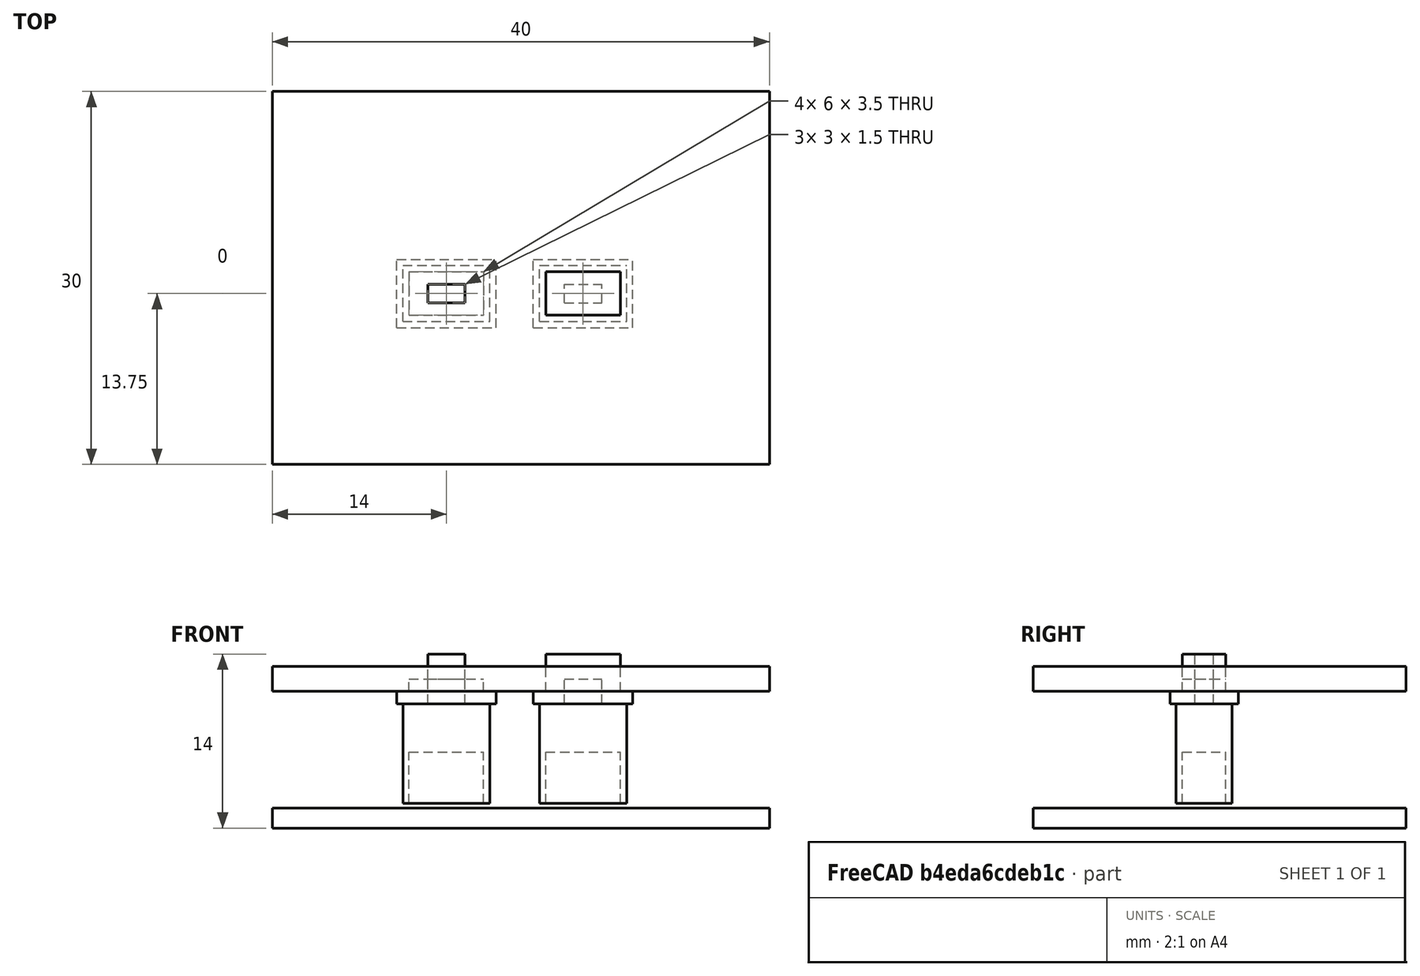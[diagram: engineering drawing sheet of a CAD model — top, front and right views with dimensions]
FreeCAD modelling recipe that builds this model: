
FCSTD DOCUMENT  (FreeCAD 0.15R4671 (Git))
Label: Button_V04
License: All rights reserved
LicenseURL: http://en.wikipedia.org/wiki/All_rights_reserved
objects: Part::Box×19, Part::Cut×6, Part::MultiFuse×5, Mesh::Feature×3
note: 30 computed .brp shape members not serialized (recipe doc carries the construction recipe); baked Part::Feature solids carry a one-line shape summary decoded from their .brp

FEATURE [Part::Box] Box  label="PCB"
  Height = 1.6
  Length = 40
  Width = 30
FEATURE [Mesh::Feature] Button
  Placement = pos=(8,30,0) rot=(1,0,0;1.5708rad)
FEATURE [Mesh::Feature] Button_TC_1101T_C_A_B  label="Button_TC-1101T-C-A-B_001"
  Placement = pos=(11,12,1.6) rot=(0,0,1;0rad)
FEATURE [Part::Box] Box001  label="Cube"
  Height = 4.5
  Length = 6
  Placement = pos=(11,12,1.6) rot=(0,0,1;0rad)
  Width = 3.5
FEATURE [Part::Box] Box002  label="Cube001"
  Height = 8
  Length = 7
  Placement = pos=(10.5,11.5,2) rot=(0,0,1;0rad)
  Width = 4.5
FEATURE [Part::Cut] Cut
  Base = -> Box002
  Tool = -> Box001
FEATURE [Part::Box] Box003  label="Cube002"
  Height = 2
  Length = 3
  Placement = pos=(12.5,13,10) rot=(0,0,1;0rad)
  Width = 1.5
FEATURE [Part::MultiFuse] Fusion  label="Button_Extn001"
  Shapes = -> [Cut,Box003]
FEATURE [Part::Box] Box004  label="Top_Cover"
  Height = 2
  Length = 40
  Placement = pos=(0,0,11) rot=(0,0,1;0rad)
  Width = 30
FEATURE [Part::Box] Box005  label="Cube003"
  Height = 2
  Length = 6
  Placement = pos=(11,12,10) rot=(0,0,1;0rad)
  Width = 3.5
FEATURE [Part::Box] Box006  label="Cube004"
  Height = 1
  Length = 8
  Placement = pos=(10,11,10) rot=(0,0,1;0rad)
  Width = 5.5
FEATURE [Part::Box] Box007  label="Cube005"
  Height = 2
  Length = 3
  Placement = pos=(12.5,13,12) rot=(0,0,1;0rad)
  Width = 1.5
FEATURE [Part::Box] Box008  label="Cube006"
  Height = 2
  Length = 3
  Placement = pos=(12.5,13,10) rot=(0,0,1;0rad)
  Width = 1.5
FEATURE [Part::MultiFuse] Fusion001
  Shapes = -> [Box005,Box006,Box007]
FEATURE [Part::Cut] Cut001  label="Membrane_SW001"
  Base = -> Fusion001
  Tool = -> Box008
FEATURE [Part::Box] Box009  label="Cube007"
  Height = 2
  Length = 6
  Placement = pos=(11,12,10) rot=(0,0,1;0rad)
  Width = 3.5
FEATURE [Part::Box] Box010  label="Cube008"
  Height = 1
  Length = 8
  Placement = pos=(10,11,10) rot=(0,0,1;0rad)
  Width = 5.5
FEATURE [Part::Box] Box011  label="Cube009"
  Height = 2
  Length = 3
  Placement = pos=(12.5,13,12) rot=(0,0,1;0rad)
  Width = 1.5
FEATURE [Part::MultiFuse] Fusion002
  Shapes = -> [Box009,Box010,Box011]
FEATURE [Part::Cut] Cut002  label="Top_"
  Base = -> Box004
  Tool = -> Fusion002
FEATURE [Mesh::Feature] Button_TC_1101T_C_A_B001  label="Button_TC-1101T-C-A-B_002"
  Placement = pos=(22,12,1.6) rot=(0,0,1;0rad)
FEATURE [Part::Box] Box012  label="Cube010"
  Height = 4.5
  Length = 6
  Placement = pos=(22,12,1.6) rot=(0,0,1;0rad)
  Width = 3.5
FEATURE [Part::Box] Box013  label="Cube011"
  Height = 8
  Length = 7
  Placement = pos=(21.5,11.5,2) rot=(0,0,1;0rad)
  Width = 4.5
FEATURE [Part::Cut] Cut003
  Base = -> Box013
  Tool = -> Box012
FEATURE [Part::Box] Box014  label="Cube012"
  Height = 2
  Length = 3
  Placement = pos=(23.5,13,10) rot=(0,0,1;0rad)
  Width = 1.5
FEATURE [Part::MultiFuse] Fusion003  label="Button_Extn002"
  Shapes = -> [Cut003,Box014]
FEATURE [Part::Box] Box015  label="Cube013"
  Height = 3
  Length = 6
  Placement = pos=(22,12,11) rot=(0,0,1;0rad)
  Width = 3.5
FEATURE [Part::Box] Box016  label="Cube014"
  Height = 1
  Length = 8
  Placement = pos=(21,11,10) rot=(0,0,1;0rad)
  Width = 5.5
FEATURE [Part::Box] Box017  label="Cube015"
  Height = 2
  Length = 3
  Placement = pos=(23.5,13,10) rot=(0,0,1;0rad)
  Width = 1.5
FEATURE [Part::MultiFuse] Fusion004
  Shapes = -> [Box015,Box016]
FEATURE [Part::Cut] Cut004  label="Membrane_SW002"
  Base = -> Fusion004
  Tool = -> Box017
FEATURE [Part::Box] Box018  label="Cube016"
  Height = 3
  Length = 6
  Placement = pos=(22,12,11) rot=(0,0,1;0rad)
  Width = 3.5
FEATURE [Part::Cut] Cut005  label="Top___"
  Base = -> Cut002
  Tool = -> Box018
